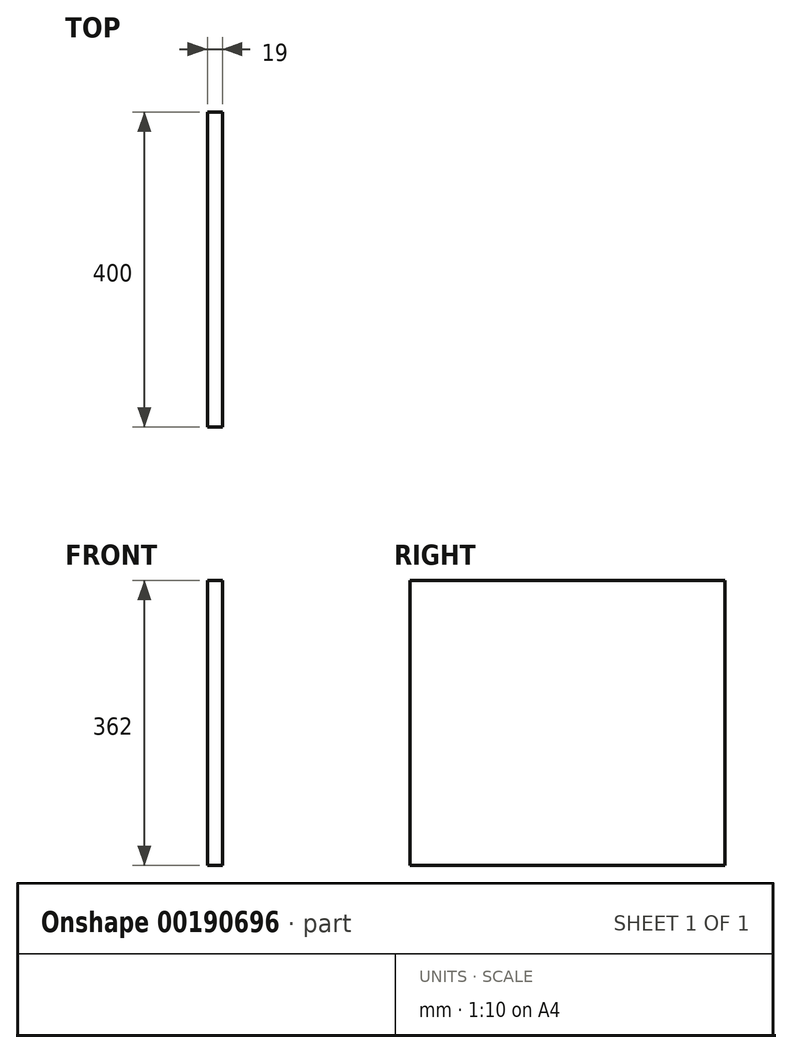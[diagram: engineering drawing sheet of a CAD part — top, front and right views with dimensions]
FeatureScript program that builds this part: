
annotation { "Feature Type Name" : "Feature", "Feature Type Description" : "" }
export const myFeature = defineFeature(function(context is Context, id is Id, definition is map)
    precondition{}
    {
        {
            var Q0;
            Q0=qCreatedBy(makeId("Right.planeOp"),FACE);
            var sketch = newSketch(context, id + "F0", { "sketchPlane" : qUnion([Q0])});
            skLineSegment(sketch, "E0.bottom", {"start": v(-180.62, 197.68) * mm, "end": v(219.38, 197.68) * mm});
            skLineSegment(sketch, "E0.top", {"start": v(-180.62, -164.32) * mm, "end": v(219.38, -164.32) * mm});
            skLineSegment(sketch, "E0.left", {"start": v(-180.62, 197.68) * mm, "end": v(-180.62, -164.32) * mm});
            skLineSegment(sketch, "E0.right", {"start": v(219.38, 197.68) * mm, "end": v(219.38, -164.32) * mm});
            skSolve(sketch);
        }
        {
            var Q0;
            Q0 = qSketchRegion(id + "F0", true);
            extrude(context, id + "F1", {"entities" : qUnion([Q0]), "depth" : 19 * mm});
        }
    });
